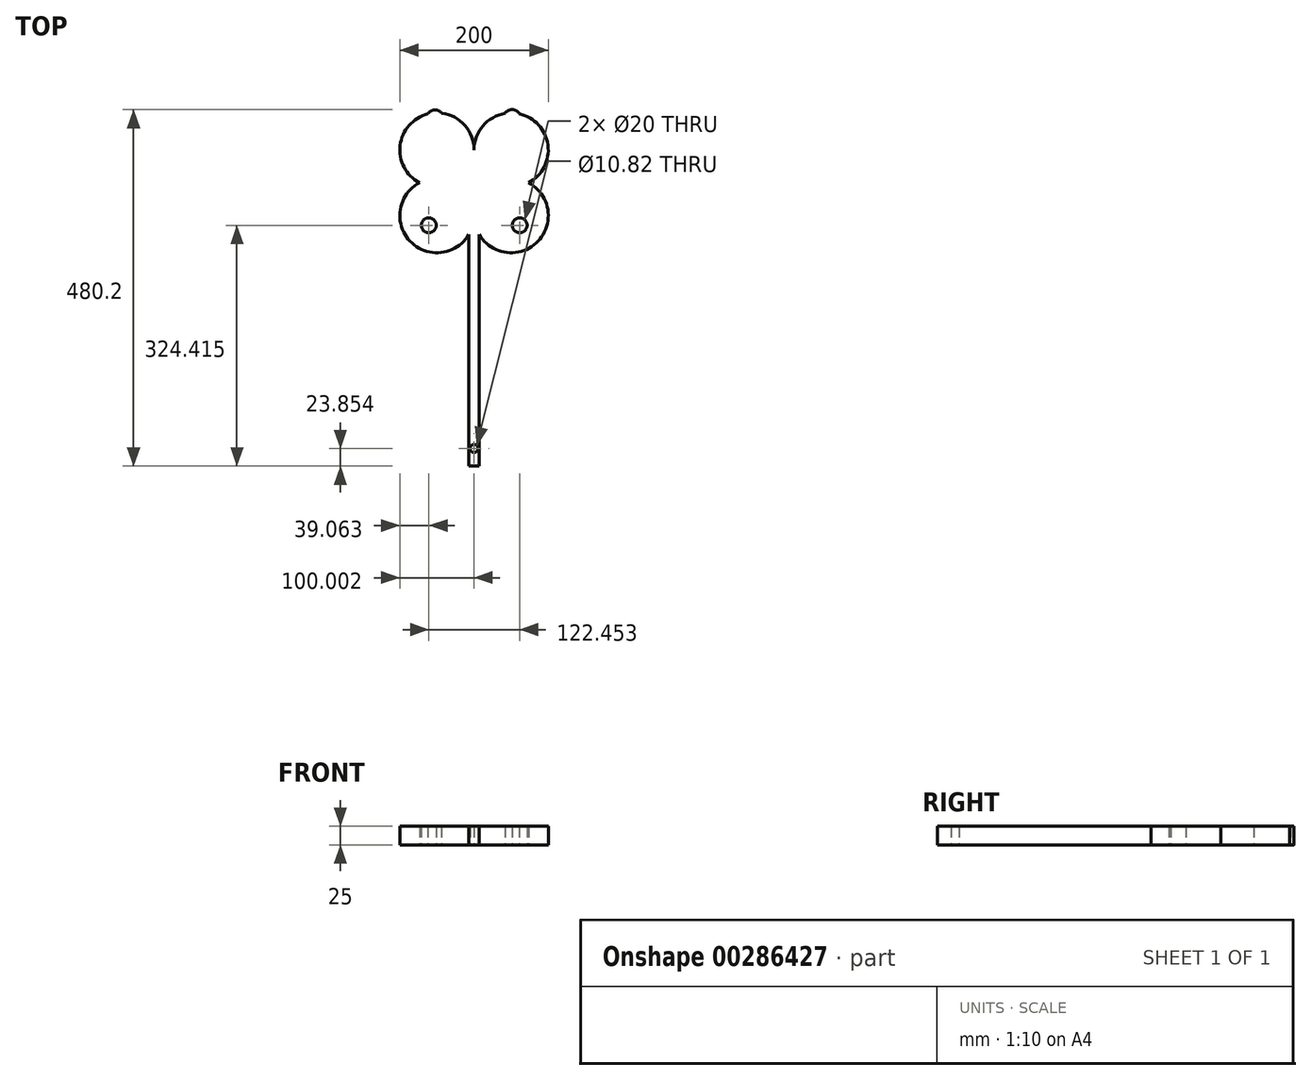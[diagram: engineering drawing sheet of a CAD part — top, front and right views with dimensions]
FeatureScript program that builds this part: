
annotation { "Feature Type Name" : "Feature", "Feature Type Description" : "" }
export const myFeature = defineFeature(function(context is Context, id is Id, definition is map)
    precondition{}
    {
        {
            var Q0;
            Q0=qCreatedBy(makeId("Top.planeOp"),FACE);
            var sketch = newSketch(context, id + "F0", { "sketchPlane" : qUnion([Q0])});
            skPoint(sketch, "E0.visualSharp", {"position": v(-170.23, -1.01) * mm});
            skPoint(sketch, "E1.visualSharp", {"position": v(-154.03, -3.73) * mm});
            skPoint(sketch, "E2.center.orphan", {"position": v(-127.81, -4.64) * mm});
            skPoint(sketch, "E3.end.orphan", {"position": v(-143.12, 0) * mm});
            skPoint(sketch, "E4.right.end.orphan", {"position": v(-127.81, 3.4) * mm});
            skPoint(sketch, "E4.bottom.end.orphan", {"position": v(-127.81, -12.68) * mm});
            skArc(sketch, "E5", {"start": v(-15.96, 45.2) * mm, "mid": v(-28.4, 78.2) * mm, "end": v(-59.52, 94.79) * mm});
            skArc(sketch, "E6", {"start": v(-15.96, -43.16) * mm, "mid": v(59.82, -86) * mm, "end": v(57.46, 1.02) * mm});
            skArc(sketch, "E7", {"start": v(-89.37, 1.02) * mm, "mid": v(-91.74, -86) * mm, "end": v(-15.96, -43.16) * mm});
            skArc(sketch, "E8.trimOffspring", {"start": v(57.46, 1.02) * mm, "mid": v(83.6, 51.78) * mm, "end": v(45.12, 93.96) * mm});
            skLineSegment(sketch, "E9.bottom", {"start": v(-56.96, 45.2) * mm, "end": v(25.04, 45.2) * mm});
            skLineSegment(sketch, "E9.top", {"start": v(-56.96, -43.16) * mm, "end": v(25.04, -43.16) * mm});
            skLineSegment(sketch, "E9.left", {"start": v(-65.96, 36.2) * mm, "end": v(-65.96, -34.16) * mm});
            skLineSegment(sketch, "E9.right", {"start": v(34.04, 36.2) * mm, "end": v(34.04, -34.16) * mm});
            skArc(sketch, "E10.filletArc", {"start": v(-56.96, 45.2) * mm, "mid": v(-63.32, 42.57) * mm, "end": v(-65.96, 36.2) * mm});
            skArc(sketch, "E11.filletArc", {"start": v(34.04, 36.2) * mm, "mid": v(31.4, 42.57) * mm, "end": v(25.04, 45.2) * mm});
            skArc(sketch, "E12.filletArc", {"start": v(25.04, -43.16) * mm, "mid": v(31.4, -40.52) * mm, "end": v(34.04, -34.16) * mm});
            skArc(sketch, "E13.filletArc", {"start": v(-65.96, -34.16) * mm, "mid": v(-63.32, -40.52) * mm, "end": v(-56.96, -43.16) * mm});
            skPoint(sketch, "E14.centerSnap0", {"position": v(59.82, 88.04) * mm});
            skPoint(sketch, "E14.center.orphan", {"position": v(35.25, 88.04) * mm});
            skLineSegment(sketch, "E15.left", {"start": v(-8.96, -68.67) * mm, "end": v(-8.96, -234.5) * mm});
            skLineSegment(sketch, "E15.right", {"start": v(-22.96, -68.67) * mm, "end": v(-22.96, -234.5) * mm});
            skPoint(sketch, "E16.orphan", {"position": v(-8.96, -43.16) * mm});
            skPoint(sketch, "E15.bottom.end.orphan", {"position": v(-22.96, -43.16) * mm});
            skCircle(sketch, "E17", {"center": v(-76.9, -56.25) * mm, "radius": 10 * mm});
            skCircle(sketch, "E18", {"center": v(45.56, -56.25) * mm, "radius": 10 * mm});
            skArc(sketch, "E19", {"start": v(-59.52, 94.79) * mm, "mid": v(-69.14, 99.04) * mm, "end": v(-78.2, 93.68) * mm});
            skArc(sketch, "E20", {"start": v(45.12, 93.96) * mm, "mid": v(35.58, 99.54) * mm, "end": v(25.74, 94.5) * mm});
            skArc(sketch, "E21.trimOffspring", {"start": v(25.74, 94.5) * mm, "mid": v(-4.13, 77.5) * mm, "end": v(-15.96, 45.2) * mm});
            skArc(sketch, "E22.trimOffspring", {"start": v(-78.2, 93.68) * mm, "mid": v(-115.6, 51.2) * mm, "end": v(-89.37, 1.02) * mm});
            skLineSegment(sketch, "E23.top", {"start": v(-8.96, -380.66) * mm, "end": v(-22.96, -380.66) * mm});
            skLineSegment(sketch, "E23.left", {"start": v(-8.96, -234.5) * mm, "end": v(-8.96, -380.66) * mm});
            skLineSegment(sketch, "E23.right", {"start": v(-22.96, -234.5) * mm, "end": v(-22.96, -380.66) * mm});
            skCircle(sketch, "E24", {"center": v(-15.96, -356.8) * mm, "radius": 5.41 * mm});
            skPoint(sketch, "E24.centerSnap0", {"position": v(-15.96, -380.66) * mm});
            skSolve(sketch);
        }
        {
            var Q0;
            Q0 = qSketchRegion(id + "F0", true);
            extrude(context, id + "F1", {"entities" : qUnion([Q0]), "depth" : 25 * mm});
        }
        {
            var Q0;
            Q0 = qSketchRegion(id + "F0", true);
            extrude(context, id + "F2", {"entities" : qUnion([Q0]), "operationType" : NewBodyOperationType.ADD, "depth" : 25 * mm});
        }
    });
